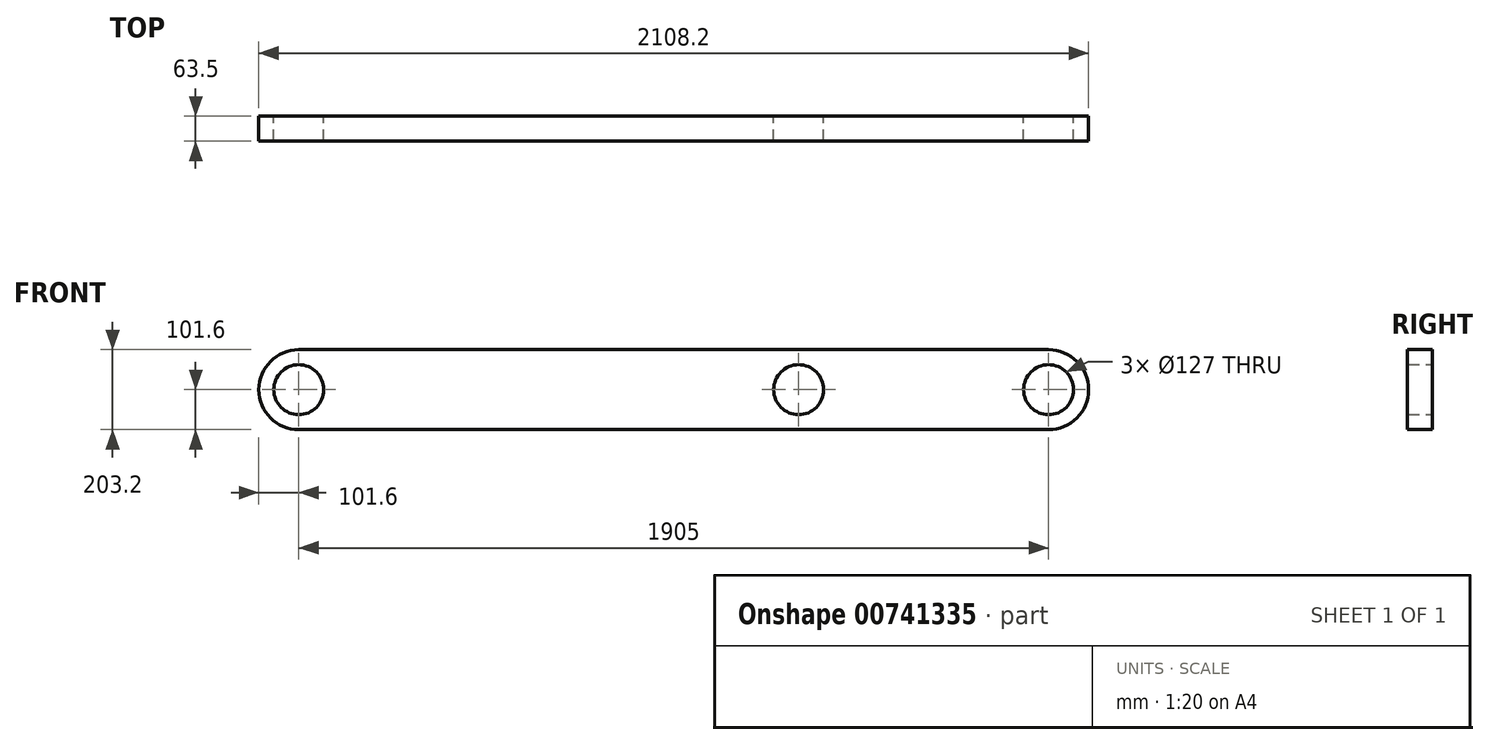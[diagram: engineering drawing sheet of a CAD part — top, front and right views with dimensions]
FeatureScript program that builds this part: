
annotation { "Feature Type Name" : "Feature", "Feature Type Description" : "" }
export const myFeature = defineFeature(function(context is Context, id is Id, definition is map)
    precondition{}
    {
        {
            var Q0;
            Q0=qCreatedBy(makeId("Front.planeOp"),FACE);
            var sketch = newSketch(context, id + "F0", { "sketchPlane" : qUnion([Q0])});
            skArc(sketch, "E0", {"start": v(-952.5, 101.6) * mm, "mid": v(-1054.1, 0) * mm, "end": v(-952.5, -101.6) * mm});
            skArc(sketch, "E1", {"start": v(952.5, -101.6) * mm, "mid": v(1054.1, 0) * mm, "end": v(952.5, 101.6) * mm});
            skLineSegment(sketch, "E2", {"start": v(-952.5, 101.6) * mm, "end": v(952.5, 101.6) * mm});
            skLineSegment(sketch, "E3", {"start": v(952.5, -101.6) * mm, "end": v(-952.5, -101.6) * mm});
            skCircle(sketch, "E4", {"center": v(-952.5, 0) * mm, "radius": 63.5 * mm});
            skCircle(sketch, "E5", {"center": v(952.5, 0) * mm, "radius": 63.5 * mm});
            skCircle(sketch, "E6", {"center": v(317.5, 0) * mm, "radius": 63.5 * mm});
            skSolve(sketch);
        }
        {
            var Q0;
            Q0 = qSketchRegion(id + "F0", true);
            extrude(context, id + "F1", {"entities" : qUnion([Q0]), "endBound" : BoundingType.SYMMETRIC, "depth" : 63.5 * mm, "offsetDistance" : 25.4 * mm});
        }
    });
